# Revit family: Roof_DSpout-Cover_1775
name_source: partatom
category: Plumbing Fixtures
revit_build: Autodesk Revit MEP 2012 (Build: 20110309_2315(x64)
units: mm (PartAtom-declared; Revit-internal decimal feet)

## types (10) — shared parameters
04 CSI = 22 14 35
95 CSI = 15165
Assembly Code = D2040200
Default Elevation = 48"
Description = Stainless Steel Housing and Cover
Manufacturer = Jay R. Smith Mfg. Co.
Material = Stainless Steel
Material Finish = Stainless Steel
Model = 1775
OmniClass Code = 22-22 14 26 13
OmniClass Title = Roof Drains
Product URL = http://www.jrsmith.com
Technical and Installation = http://www.jrsmith.com
URL = http://www.jrsmith.com
Warranty = 1 year material and workmanship

## per-type parameters (varying)
| type | A Dia | B Dia | C Dia | Cylinder Thickness | D Dia | E Dia | Pipe Radius | Weight (lb) |
| 1775-02 | 2" | 3 1/2" | 4 1/2" | 1/8" | 7 11/16" | 6" | 1" | 3.6 |
| 1775-03 | 3" | 3 1/2" | 4 1/2" | 1/4" | 7 11/16" | 6" | 1 1/2" | 3.6 |
| 1775-06 | 6" | 6 11/16" | 7 11/16" | 1/8" | 10 7/8" | 9" | 3" | 4.95 |
| 1775-08 | 8" | 8 11/16" | 9 11/16" | 1/8" | 12 7/8" | 11 1/4" | 4" | 6.4 |
| 1775-10 | 10" | 10 13/16" | 11 13/16" | 1/8" | 15" | 13 1/2" | 5" | 8.85 |
| 1775-05 | 5" | 5 5/8" | 6 5/8" | 1/8" | 9 13/16" | 8 1/4" | 2 1/2" | 4.2 |
| 1775-12 | 12" | 12 13/16" | 13 13/16" | 1/8" | 17" | 15 1/2" | 6" | 10.56 |
| 1775-0150 | 1 1/2" | 3 1/2" | 4 1/2" | 1/4" | 7 11/16" | 6" | 3/4" | 3.6 |
| 1775-04 | 4" | 4 9/16" | 5 9/16" | 1/4" | 8 3/4" | 7 1/8" | 2" | 4.6 |
| 1775-15 | 15" | 16" | 16 15/16" | 1/8" | 20 1/8" | 18 1/2" | 7 1/2" | 13.55 |

## geometry (parser evidence)
native form markers: Blend x6, Sweep x3
no freeform markers — native parametric forms only
